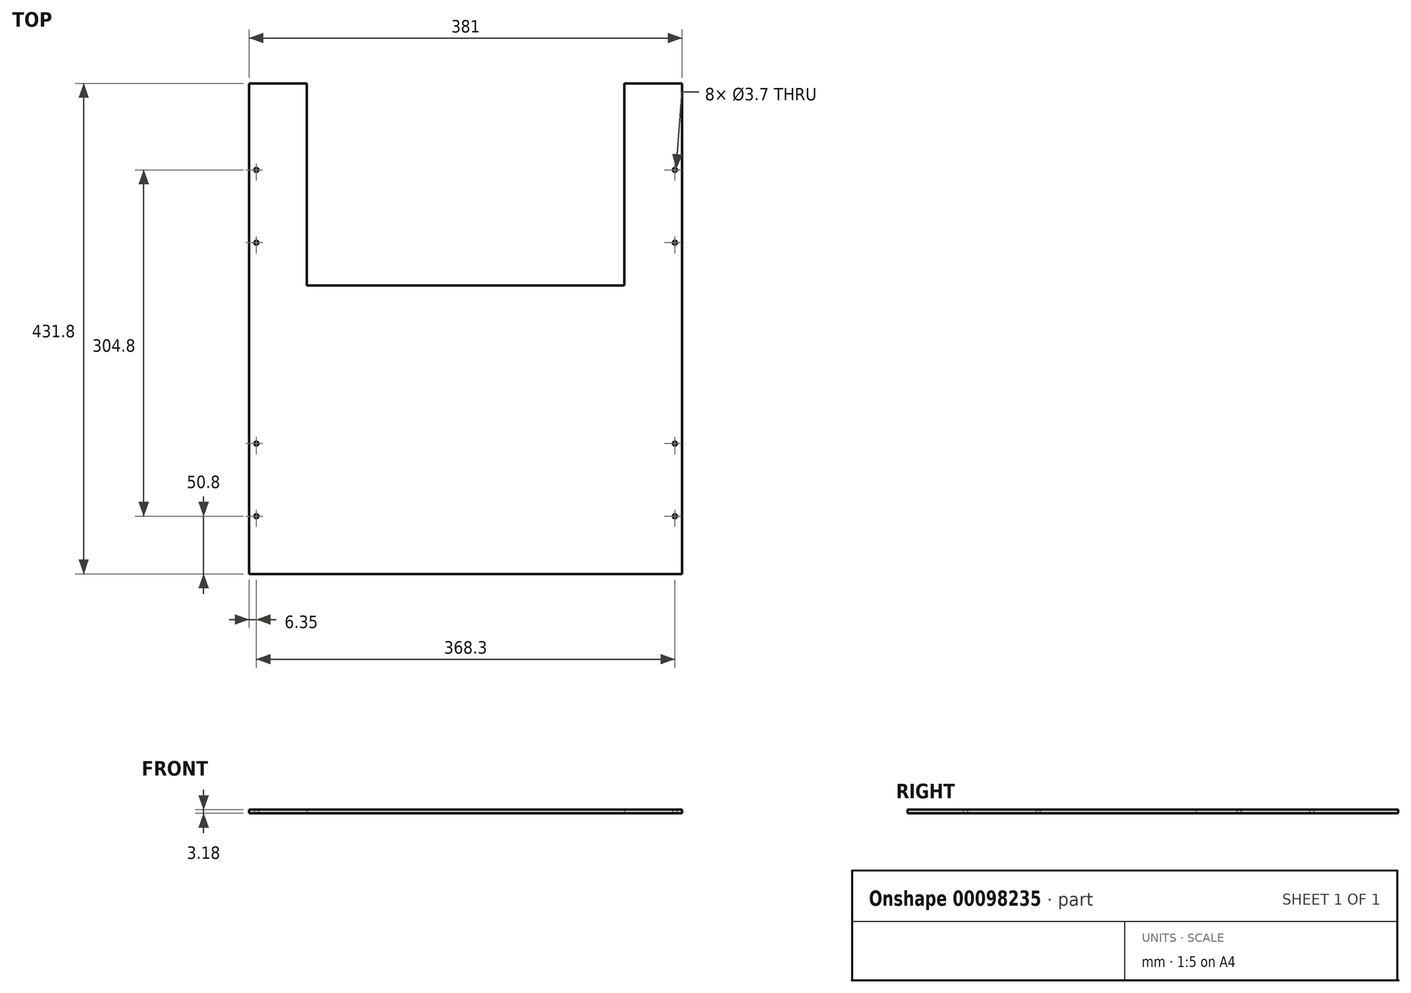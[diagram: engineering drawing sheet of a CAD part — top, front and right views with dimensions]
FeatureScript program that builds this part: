
annotation { "Feature Type Name" : "Feature", "Feature Type Description" : "" }
export const myFeature = defineFeature(function(context is Context, id is Id, definition is map)
    precondition{}
    {
        {
            var Q0;
            Q0=qCreatedBy(makeId("Top.planeOp"),FACE);
            var sketch = newSketch(context, id + "F0", { "sketchPlane" : qUnion([Q0])});
            skLineSegment(sketch, "E0.bottom", {"start": v(190.5, 215.9) * mm, "end": v(-190.5, 215.9) * mm});
            skLineSegment(sketch, "E0.top", {"start": v(190.5, -215.9) * mm, "end": v(-190.5, -215.9) * mm});
            skLineSegment(sketch, "E0.left", {"start": v(190.5, 215.9) * mm, "end": v(190.5, -215.9) * mm});
            skLineSegment(sketch, "E0.right", {"start": v(-190.5, 215.9) * mm, "end": v(-190.5, -215.9) * mm});
            skPoint(sketch, "E0.middle", {"position": v(0, 0) * mm});
            skPoint(sketch, "E1", {"position": v(-184.15, 139.7) * mm});
            skPoint(sketch, "E2", {"position": v(-184.15, 75.7) * mm});
            skPoint(sketch, "E3", {"position": v(-184.15, -101.1) * mm});
            skPoint(sketch, "E4", {"position": v(-184.15, -165.1) * mm});
            skPoint(sketch, "E5", {"position": v(184.15, -101.1) * mm});
            skPoint(sketch, "E6", {"position": v(184.15, -165.1) * mm});
            skPoint(sketch, "E7", {"position": v(184.15, 139.7) * mm});
            skPoint(sketch, "E8", {"position": v(184.15, 75.7) * mm});
            skCircle(sketch, "E9", {"center": v(-184.15, 139.7) * mm, "radius": 1.85 * mm});
            skCircle(sketch, "E10", {"center": v(-184.15, 75.7) * mm, "radius": 1.85 * mm});
            skCircle(sketch, "E11", {"center": v(-184.15, -101.1) * mm, "radius": 1.85 * mm});
            skCircle(sketch, "E12", {"center": v(-184.15, -165.1) * mm, "radius": 1.85 * mm});
            skCircle(sketch, "E13", {"center": v(184.15, -101.1) * mm, "radius": 1.85 * mm});
            skCircle(sketch, "E14", {"center": v(184.15, -165.1) * mm, "radius": 1.85 * mm});
            skCircle(sketch, "E15", {"center": v(184.15, 139.7) * mm, "radius": 1.85 * mm});
            skCircle(sketch, "E16", {"center": v(184.15, 75.7) * mm, "radius": 1.85 * mm});
            skLineSegment(sketch, "E17.bottom", {"start": v(-139.7, 215.9) * mm, "end": v(139.7, 215.9) * mm});
            skLineSegment(sketch, "E17.top", {"start": v(-139.7, 38.1) * mm, "end": v(139.7, 38.1) * mm});
            skLineSegment(sketch, "E17.left", {"start": v(-139.7, 215.9) * mm, "end": v(-139.7, 38.1) * mm});
            skLineSegment(sketch, "E17.right", {"start": v(139.7, 215.9) * mm, "end": v(139.7, 38.1) * mm});
            skSolve(sketch);
        }
        {
            var Q0;
            Q0=makeQuery(id+"F0.imprint","IMPRINT",FACE,{"disambiguationData":[TD([[makeQuery(id+"F0.imprint","IMPRINT",EDGE,{"derivedFrom":sQuery(id+"F0.wireOp",EDGE,"E0.top")}),-1.0]])]});
            extrude(context, id + "F1", {"entities" : qUnion([Q0]), "depth" : 3.17 * mm});
        }
    });
